# Revit family: LWPLIFE-PRO-XX-WM_Lighting_Non-Hosted_R20
name_source: partatom
category: Lighting Fixtures
units: mm (PartAtom-declared; Revit-internal decimal feet)

## family parameters
Always vertical = Yes
Cut with Voids When Loaded = No
Light Source = Yes
OmniClass Number = 23.80.70.00
OmniClass Title = Lighting
Part Type = Normal
Room Calculation Point = No
Round Connector Dimension = Use Diameter
Shared = No
Work Plane-Based = No

## types (15) — shared parameters
AS2293 Classification = C0=D50 C90=D50
Applicable Standards = AS/NZS3820, CISPR15, AS/NZS2293.3
Battery = 3.3V 5000mAh
Battery Type = Lithium Nanophosphate
Charging Method = Intelligent Current Limited Constant Voltage
Color Filter = 16777215
Diffuser = Clear Toughened Glass
Dimming Lamp Color Temperature Shift = <None>
Emit Shape Visible in Rendering = No
IK Rating = IK10
IP Rating = IP65
Manufacturer = Clevertronics
Operating Temperature = 0˚C to 40˚C
Operating Voltage = 240V AC; 50Hz
Photometric Web File = ll20550-r01 - LWPLIFEM-PRO-ZW(WM).IES
Tilt Angle = 0.00°
zero-valued in all types: Default Elevation

## per-type parameters (varying)
| type | Construction | Description | Dimensions (L x W x H) | Emergency Lumen Output | Keynote | Lamp | MIC Number | Model | Mounting | Operating Mode | Power Consumption | Power Consumption (Standby - Lamp Off) | Replacement Battery | Replacement Emergency Driver | Replacement Emergency Lamp | Replacement Item | Testing System | Weight |
| LWPLIFE-PRO-ZW-WM-BLK | Die Cast Aluminium Body, Stainless Steel Screws, | Lifelight Pro, WM, NM, ZW,L10, Ligman, D50, Blk | 287mm x 186mm x 260mm | 326 lumens | L10 Optimum LifeLight PRO, IP65 Wall Mounted Emergency Luminaire, Black | 2 x 3W LED (Lifetime warranty on the Lamp head and loom Assembly) | AUT01120210001 | LWPLIFE-PRO-ZW-WM-BLK | Wall Mount | Non-maintained | 3.0 Watts | 0.7 Watts | 1530230 BATTERY:L10 3.3V 5AH. 200mm lead.no Brkt | AUM01170070101   LLIFE-PRO-CKIT-ZW-NP     Lifelight Pro,Control Only,Batten, ZW, L10, OWC | 1100817 Lifelight Pro Head Assembly, Round, LT, Blk, Gen 2 | 8001450 PCA:Powerline Node ZW, #CT10310-A6 | Zoneworks computerised testing | 5kg |
| LWPLIFE-PRO-WM-MSLV | Die Cast Aluminium Body, Stainless Steel Screws |  | 287mm x 186mm x 260mm |  | L10 Optimum LifeLight PRO, Wall Mounted Emergency, Silver | Dual LED (Lifetime Warranty on the Lamp Head and Loom Assembly) | AUT01310550001 | LWPLIFE-PRO-WM-MSLV | Wall Mount | Non-maintained | 2.7 Watts | 0.4 Watts | 1530230 | AUM01370120001LLIFE-PRO-CKIT-NP | 1100869 |  | Clevertest Plus Enabled (not activated by default) | 5kg |
| LWPLIFE-PRO-HV-WM-MSLV | Die Cast Aluminium Body, Stainless Steel Screws |  | 186mm Diameter x 289mm Height |  | L10 Optimum LifeLight PRO, Wall Mounted Emergency, Silver | Dual LED (Lifetime Warranty on the Lamp Head and Loom Assembly) | AUT01810520001 | LWPLIFE-PRO-HV-WM-MSLV | Ceiling Mount | Non-maintained | 3.0 Watts | 0.7 Watts | 1530230 | AUM01870170001 LLIFE-PRO-CKIT-HVEXTA-NP | 1100869 | 8003191 | Zoneworks XT Hive (RF) | 5kg |
| LWPLIFE-PRO-DALI-WM-MSLV | Die Cast Aluminium Body, Stainless Steel Screws |  | 287mm x 186mm x 260mm |  | L10 Optimum LifeLight PRO, Wall Mounted Emergency, Silver, DALI Registered | Dual LED (Lifetime Warranty on the Lamp Head and Loom Assembly) | AUT01210680002 | LWPLIFE-PRO-DALI-WM-MSLV | Wall Mount | Non-maintained | 3.0 Watts | 0.7 Watts | 1530230 | AUM01270240002 LLIFE-PRO-CKIT-DALI-NP | 1100869 |  | DALI Registered | 5kg |
| LWPLIFE-PRO-WM-BLK | Die Cast Aluminium Body, Stainless Steel Screws |  | 287mm x 186mm x 260mm |  | L10 Optimum LifeLight PRO, IP65 Wall Mounted Emergency Luminaire, Black, Clevertest Plus Enabled (Not activated by default) | 2 x 3W LED (Lifetime warranty on the Lamp head and loom Assembly) | AUT01320040002 | LWPLIFE-PRO-WM-BLK | Wall Mount | Non-maintained | 2.7 Watts | 0.4 Watts | 1530230 | AUM01370120001 LLIFE-PRO-CKIT-NP | 1100817 |  | Enabled with Clevertest Plus | 5kg |
| LWPLIFE-PRO-WM-WHT | Die Cast Aluminium Body, Stainless Steel Screws |  | 287mm x 186mm x 260mm |  | L10 Optimum LifeLight PRO, IP65 Wall Mounted Emergency Luminaire, White, Clevertest Plus Enabled (Not activated by default) | 2 x 3W LED (Lifetime warranty on the Lamp head and loom Assembly) | AUT01320060001 | LWPLIFE-PRO-WM-WHT | Wall Mount | Non-maintained | 2.7 Watts | 0.4 Watts | 1530230 | AUM01370120001 LLIFE-PRO-CKIT-NP | 1100838 |  | Enabled with Clevertest Plus | 5kg |
| LWPLIFE-PRO-WM-DGRY | Die Cast Aluminium Body, Stainless Steel Screws |  | 287mm x 186mm x 260mm |  | L10 Optimum LifeLight PRO, IP65 Wall Mounted Emergency Luminaire, Dark Grey, Clevertest Plus Enabled (Not activated by default) | 2 x 3W LED (Lifetime warranty on the Lamp head and loom Assembly) | AUT01320350001 | LWPLIFE-PRO-WM-DGRY | Wall Mount | Non-maintained | 2.7 Watts | 0.4 Watts | 1530230 | AUM01370120001 LLIFE-PRO-CKIT-NP | 1100838 |  | Enabled with Clevertest Plus | 5kg |
| LWPLIFE-PRO-WM-SLV | Die Cast Aluminium Body, Stainless Steel Screws | Lifelight Pro,WM,NM,L10,Ligman,Matt Silver,CTP,D50 | 287mm x 186mm x 260mm |  | L10 Optimum LifeLight PRO, IP65 Wall Mounted Emergency Luminaire, Silver,Clevertest Plus Enabled (Not activated by default) | 2 x 3W LED (Lifetime warranty on the Lamp head and loom Assembly) | AUT01320050001 | LWPLIFE-PRO-WM-SLV | Wall Mount | Non-maintained | 2.7 Watts | 0.4 Watts | 1530230 | AUM01370120001 LLIFE-PRO-CKIT-NP | 1100838 |  | Enabled with Clevertest Plus | 5kg |
| LWPLIFE-PRO-HVG-WM-BLK | Die Cast Aluminium Body, Stainless Steel Screws | Lifelight Pro, WM, NM, HVG, L10, Ligman, White | 287mm x 186mm x 260mm |  | Lifelight Pro IP65 Weatherproof Cylinder Emergency, Wall Mount, L10 Nanophosphate, Zoneworks XT Hive 2.4GHz, White | 2 x 3W LED (Lifetime warranty on the Lamp head and loom Assembly) | AUT01920030001 | LWPLIFE-PRO-HVG-WM-WHT | Wall Mount | Non-maintained | 3.0 Watts | 0.7 Watts | 1530230 | AUM01970080002 LLIFE-PRO-CKIT-HVGEXTA-NP | 1100869 |  | Zoneworks XT HIVE (RF) | 5kg |
| LWPLIFE-PRO-DALI-WM-WHT | Die Cast Aluminium Body, Stainless Steel Screws | Lifelight Pro,WM, NM, Dali Reg, L10, Ligman, White | 287mm x 186mm x 260mm |  | L10 Lithium Nanophosphate LifeLight PRO, IP65 wall mounted Emergency, White | Dual LED (Lifetime warranty on the lamp head and loom assembly) | AUT01220280002 | LWPLIFE-PRO-DALI-WM-WHT | Wall Mount | Non-maintained | 3.0 Watts | 0.7 Watts | 1530230 | AUM01370120001 LLIFE-PRO-CKIT-NP | 1100835 |  | DALI Registered | 5kg |
| LWPLIFE-PRO-DALI-WM-BLK | Die Cast Aluminium Body, Stainless Steel Screws | Lifelight Pro, WM, NM, Dali Reg, L10, Ligman, Blk | 287mm x 186mm x 260mm |  | L10 Lithium Nanophosphate LifeLight PRO, IP65 wall mounted Emergency Light, Black | 2 x 3W LED (Lifetime warranty on the Lamp head and loom Assembly) | AUT01220170102 | LWPLIFE-PRO-DALI-WM-BLK | Wall Mount | Non-maintained | 3.0 Watts | 0.7 Watts | 1530230 | AUM01270240002 - LLIFE-PRO-CKIT-DALI-NP | 1100872 |  | DALI Registered | 5kg |
| LWPLIFE-PRO-HV-WM-WHT | Die Cast Aluminium Body, Stainless Steel Screws | Lifelight Pro, WM, NM, HV, L10, Ligman, White | 287mm x 186mm x 260mm |  | L10 Optimum LifeLight PRO, IP65 Wall Mounted Emergency Luminaire, White | 2 x 3W LED (Lifetime warranty on the Lamp head and loom Assembly) | AUT01820260001 | LWPLIFE-PRO-HV-WM-WHT | Wall Mount | Non-maintained | 3.0 Watts | 0.7 Watts | 1530230 | AUM01870170001 LLIFE-PRO-CKIT-HVEXTA-NP | 1100869 |  | Zoneworks XT HIVE (RF) | 5kg |
| LWPLIFE-PRO-HV-WM-SLV | Die Cast Aluminium Body, Stainless Steel Screws | Lifelight Pro, WM, NM, HV, L10,D50,Ligman,Matt Slv | 287mm x 186mm x 260mm |  | L10 Optimum LifeLight PRO, IP65 Wall Mounted Emergency Luminaire, Silver | 2 x 3W LED (Lifetime warranty on the Lamp head and loom Assembly) | AUT01820170001 | LWPLIFE-PRO-HV-WM-SLV | Wall Mount | Non-maintained | 3.0 Watts | 0.7 Watts | 1530230 | AUM01870170001 - LLIFE-PRO-CKIT-HVEXTA-NP | 1100869 |  | Zoneworks XT HIVE (RF) | 5kg |
| LWPLIFE-PRO-HV-WM-BLK | Die Cast Aluminium Body, Stainless Steel Screws | Lifelight Pro, WM, NM, HV,L10, OWC,D50, Ligman,Blk | 287mm x 186mm x 260mm |  | L10 Optimum LifeLight PRO, IP65 Wall Mounted Emergency Luminaire, Black | 2 x 3W LED (Lifetime warranty on the Lamp head and loom Assembly) | AUT01820240001 | LWPLIFE-PRO-HV-WM-BLK | Wall Mount | Non-maintained | 3.0 Watts | 0.7 Watts | 1530230 | AUM01870520001 - LLIFE-PRO-CKIT-HVEXTA-NP-BLK | 1100872 |  | Zoneworks XT HIVE (RF) | 5kg |
| LWPLIFE-PRO-DALI-WM-BLK-UPS | Die Cast Aluminium Body, Stainless Steel Screws | Lifelight Pro, WM, NM, Dali, Gen 2,WL, Blk,UPS | 287mm x 186mm x 260mm |  | Lifelight Pro, WM, NM, Dali, Gen 2, WL, Blk, UPS | Dual LED | AUT01220400002 | LWPLIFE-PRO-DALI-WM-BLK-UPS | Wall Mount | UPS | 0.95 Watts |  |  | AUM01270480002 LLIFE-PRO-CKIT-DALI-NP-UPS | 1100872 |  |  |  |

## geometry (parser evidence)
native form markers: Sweep x2
no freeform markers — native parametric forms only
